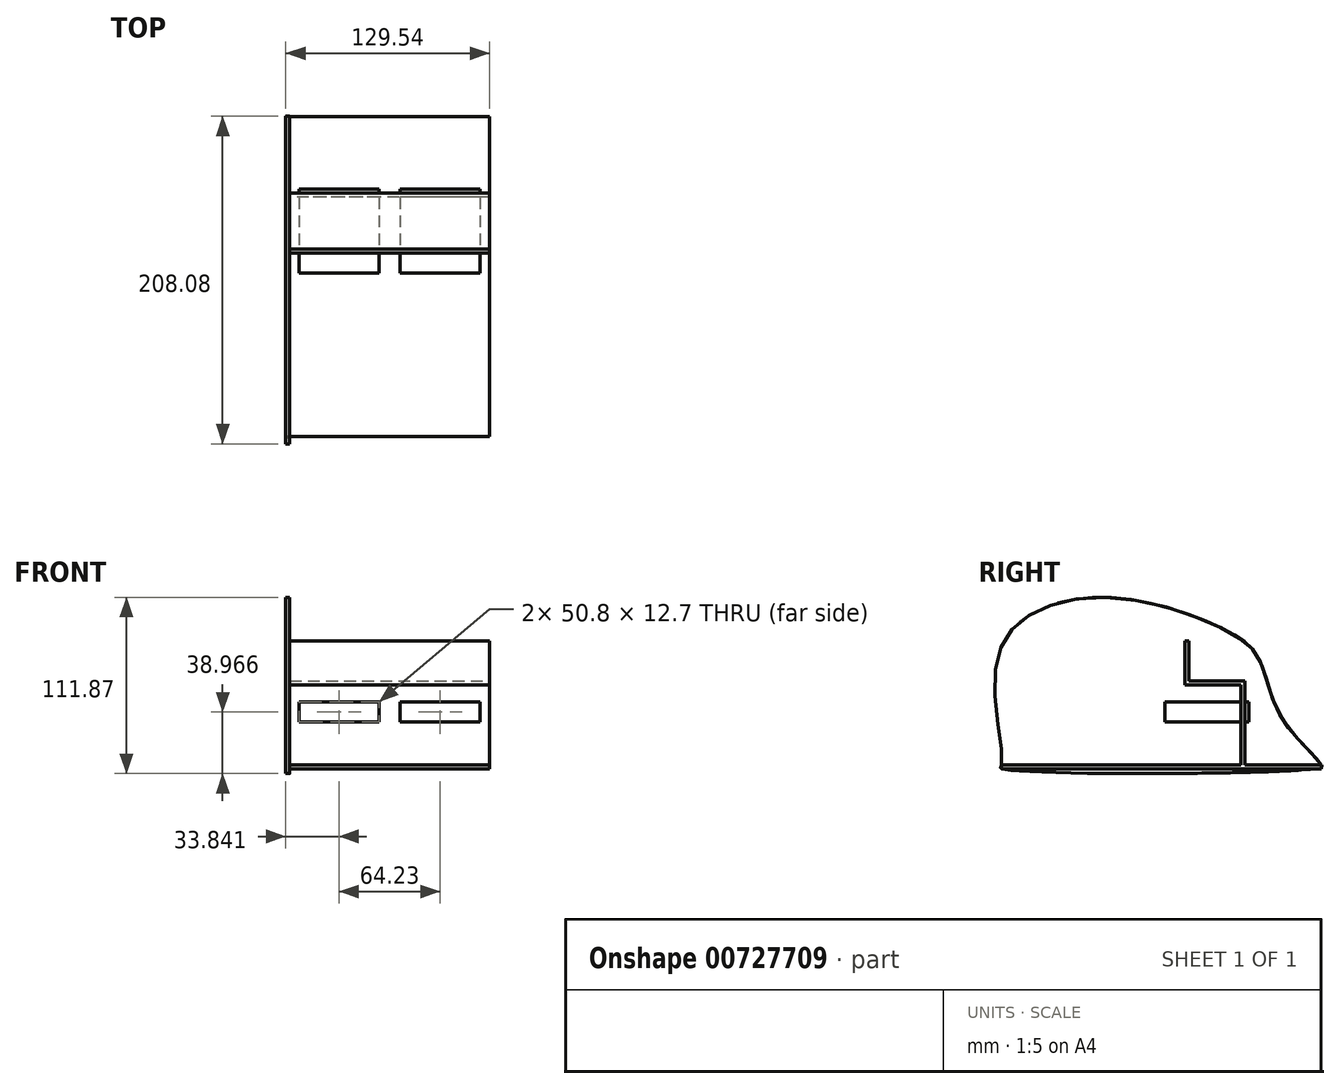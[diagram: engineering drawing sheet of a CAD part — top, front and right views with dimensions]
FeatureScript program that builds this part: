
annotation { "Feature Type Name" : "Feature", "Feature Type Description" : "" }
export const myFeature = defineFeature(function(context is Context, id is Id, definition is map)
    precondition{}
    {
        {
            var Q0;
            Q0=qCreatedBy(makeId("Top.planeOp"),FACE);
            var sketch = newSketch(context, id + "F0", { "sketchPlane" : qUnion([Q0])});
            skLineSegment(sketch, "E0.bottom", {"start": v(63.5, -101.6) * mm, "end": v(-63.5, -101.6) * mm});
            skLineSegment(sketch, "E0.top", {"start": v(63.5, 101.6) * mm, "end": v(-63.5, 101.6) * mm});
            skLineSegment(sketch, "E0.left", {"start": v(63.5, -101.6) * mm, "end": v(63.5, 101.6) * mm});
            skLineSegment(sketch, "E0.right", {"start": v(-63.5, -101.6) * mm, "end": v(-63.5, 101.6) * mm});
            skPoint(sketch, "E0.middle", {"position": v(0, 0) * mm});
            skSolve(sketch);
        }
        {
            var Q0;
            Q0 = qSketchRegion(id + "F0", true);
            extrude(context, id + "F1", {"entities" : qUnion([Q0]), "depth" : 2.54 * mm, "offsetDistance" : 25.4 * mm});
        }
        {
            var Q0;
            Q0=makeQuery(id+"F1.opExtrude","CAP_FACE",FACE,{"disambiguationData":[OSD([sQuery(id+"F0.wireOp",EDGE,"E0.bottom"),sQuery(id+"F0.wireOp",EDGE,"E0.top"),sQuery(id+"F0.wireOp",EDGE,"E0.left"),sQuery(id+"F0.wireOp",EDGE,"E0.right")])],"isStart":false});
            var sketch = newSketch(context, id + "F2", { "sketchPlane" : qUnion([Q0])});
            skLineSegment(sketch, "E1", {"start": v(63.5, 50.49) * mm, "end": v(-63.5, 50.49) * mm});
            skLineSegment(sketch, "E2", {"start": v(-63.5, 53.03) * mm, "end": v(63.5, 53.03) * mm});
            skLineSegment(sketch, "E3", {"start": v(63.5, 53.03) * mm, "end": v(63.5, 50.49) * mm});
            skLineSegment(sketch, "E4", {"start": v(-63.5, 50.49) * mm, "end": v(-63.5, 53.03) * mm});
            skSolve(sketch);
        }
        {
            var Q0;
            Q0 = qSketchRegion(id + "F2", true);
            extrude(context, id + "F3", {"entities" : qUnion([Q0]), "operationType" : NewBodyOperationType.ADD, "depth" : 50.8 * mm, "offsetDistance" : 25.4 * mm});
        }
        {
            var Q0;
            Q0=makeQuery(id+"F3.opExtrude","CAP_FACE",FACE,{"disambiguationData":[OSD([sQuery(id+"F2.wireOp",EDGE,"E1"),sQuery(id+"F2.wireOp",EDGE,"E2"),sQuery(id+"F2.wireOp",EDGE,"E3"),sQuery(id+"F2.wireOp",EDGE,"E4")])],"isStart":false});
            var sketch = newSketch(context, id + "F4", { "sketchPlane" : qUnion([Q0])});
            skLineSegment(sketch, "E5.bottom", {"start": v(63.5, 53.03) * mm, "end": v(-63.5, 53.03) * mm});
            skLineSegment(sketch, "E5.top", {"start": v(63.5, 14.93) * mm, "end": v(-63.5, 14.93) * mm});
            skLineSegment(sketch, "E5.left", {"start": v(63.5, 53.03) * mm, "end": v(63.5, 14.93) * mm});
            skLineSegment(sketch, "E5.right", {"start": v(-63.5, 53.03) * mm, "end": v(-63.5, 14.93) * mm});
            skSolve(sketch);
        }
        {
            var Q0;
            Q0 = qSketchRegion(id + "F4", true);
            var Q1;
            Q1 = qSketchRegion(id + "F0", true);
            var Q2;
            Q2 = qSketchRegion(id + "F2", true);
            extrude(context, id + "F5", {"entities" : qUnion([Q0, Q1, Q2]), "operationType" : NewBodyOperationType.ADD, "depth" : 2.54 * mm, "offsetDistance" : 25.4 * mm});
        }
        {
            var Q0;
            Q0=makeQuery(id+"F5.boolean.opBoolean","MERGE",FACE,{"derivedFrom":[makeQuery(id+"F3.boolean.opBoolean","MERGE",FACE,{"derivedFrom":[makeQuery(id+"F1.opExtrude","SWEPT_FACE",FACE,{"disambiguationData":[OSD([sQuery(id+"F0.wireOp",EDGE,"E0.right")])]}),makeQuery(id+"F3.opExtrude","SWEPT_FACE",FACE,{"disambiguationData":[OSD([sQuery(id+"F2.wireOp",EDGE,"E4")])]})]}),makeQuery(id+"F5.opExtrude","SWEPT_FACE",FACE,{"disambiguationData":[OSD([sQuery(id+"F4.wireOp",EDGE,"E5.right")])]})]});
            var sketch = newSketch(context, id + "F6", { "sketchPlane" : qUnion([Q0])});
            skFitSpline(sketch, "E6", {"points": [v(-101.6, 2.54) * mm, v(-77.33, 30.7) * mm, v(-62.9, 67.53) * mm, v(-46.02, 85.02) * mm, v(26.7, 108.34) * mm, v(88.38, 94.53) * mm, v(106.18, 54.64) * mm, v(101.6, 2.54) * mm, v(101.6, 0) * mm, v(-98.2, 0) * mm, v(-101.6, 2.54) * mm]});
            skSolve(sketch);
        }
        {
            var Q0;
            Q0 = qSketchRegion(id + "F6", true);
            extrude(context, id + "F7", {"entities" : qUnion([Q0]), "operationType" : NewBodyOperationType.ADD, "depth" : 2.54 * mm, "offsetDistance" : 25.4 * mm});
        }
        {
            var Q0;
            Q0=makeQuery(id+"F5.opExtrude","CAP_FACE",FACE,{"disambiguationData":[OSD([sQuery(id+"F4.wireOp",EDGE,"E5.bottom"),sQuery(id+"F4.wireOp",EDGE,"E5.top"),sQuery(id+"F4.wireOp",EDGE,"E5.left"),sQuery(id+"F4.wireOp",EDGE,"E5.right")])],"isStart":false});
            var sketch = newSketch(context, id + "F8", { "sketchPlane" : qUnion([Q0])});
            skLineSegment(sketch, "E7.bottom", {"start": v(63.5, 14.93) * mm, "end": v(-63.5, 14.93) * mm});
            skLineSegment(sketch, "E7.top", {"start": v(63.5, 17.47) * mm, "end": v(-63.5, 17.47) * mm});
            skLineSegment(sketch, "E7.left", {"start": v(63.5, 14.93) * mm, "end": v(63.5, 17.47) * mm});
            skLineSegment(sketch, "E7.right", {"start": v(-63.5, 14.93) * mm, "end": v(-63.5, 17.47) * mm});
            skSolve(sketch);
        }
        {
            var Q0;
            Q0 = qSketchRegion(id + "F8", true);
            extrude(context, id + "F9", {"entities" : qUnion([Q0]), "operationType" : NewBodyOperationType.ADD, "depth" : 25.4 * mm, "offsetDistance" : 25.4 * mm});
        }
        {
            var Q0;
            Q0=makeQuery(id+"F5.boolean.opBoolean","MERGE",FACE,{"derivedFrom":[makeQuery(id+"F3.opExtrude","SWEPT_FACE",FACE,{"disambiguationData":[OSD([sQuery(id+"F2.wireOp",EDGE,"E2")])]}),makeQuery(id+"F5.opExtrude","SWEPT_FACE",FACE,{"disambiguationData":[OSD([sQuery(id+"F4.wireOp",EDGE,"E5.bottom")])]})]});
            var sketch = newSketch(context, id + "F10", { "sketchPlane" : qUnion([Q0])});
            skLineSegment(sketch, "E8.bottom", {"start": v(-57.43, 42.3) * mm, "end": v(-6.63, 42.3) * mm});
            skLineSegment(sketch, "E8.top", {"start": v(-57.43, 29.6) * mm, "end": v(-6.63, 29.6) * mm});
            skLineSegment(sketch, "E8.left", {"start": v(-57.43, 42.3) * mm, "end": v(-57.43, 29.6) * mm});
            skLineSegment(sketch, "E8.right", {"start": v(-6.63, 42.3) * mm, "end": v(-6.63, 29.6) * mm});
            skLineSegment(sketch, "E9.bottom", {"start": v(6.8, 42.3) * mm, "end": v(57.6, 42.3) * mm});
            skLineSegment(sketch, "E9.top", {"start": v(6.8, 29.6) * mm, "end": v(57.6, 29.6) * mm});
            skLineSegment(sketch, "E9.left", {"start": v(6.8, 42.3) * mm, "end": v(6.8, 29.6) * mm});
            skLineSegment(sketch, "E9.right", {"start": v(57.6, 42.3) * mm, "end": v(57.6, 29.6) * mm});
            skSolve(sketch);
        }
        {
            var Q0;
            Q0 = qSketchRegion(id + "F10", true);
            extrude(context, id + "F11", {"entities" : qUnion([Q0]), "operationType" : NewBodyOperationType.ADD, "depth" : 2.54 * mm, "offsetDistance" : 25.4 * mm, "hasSecondDirection" : true, "secondDirectionOppositeDirection" : true, "secondDirectionDepth" : 50.8 * mm});
        }
    });
